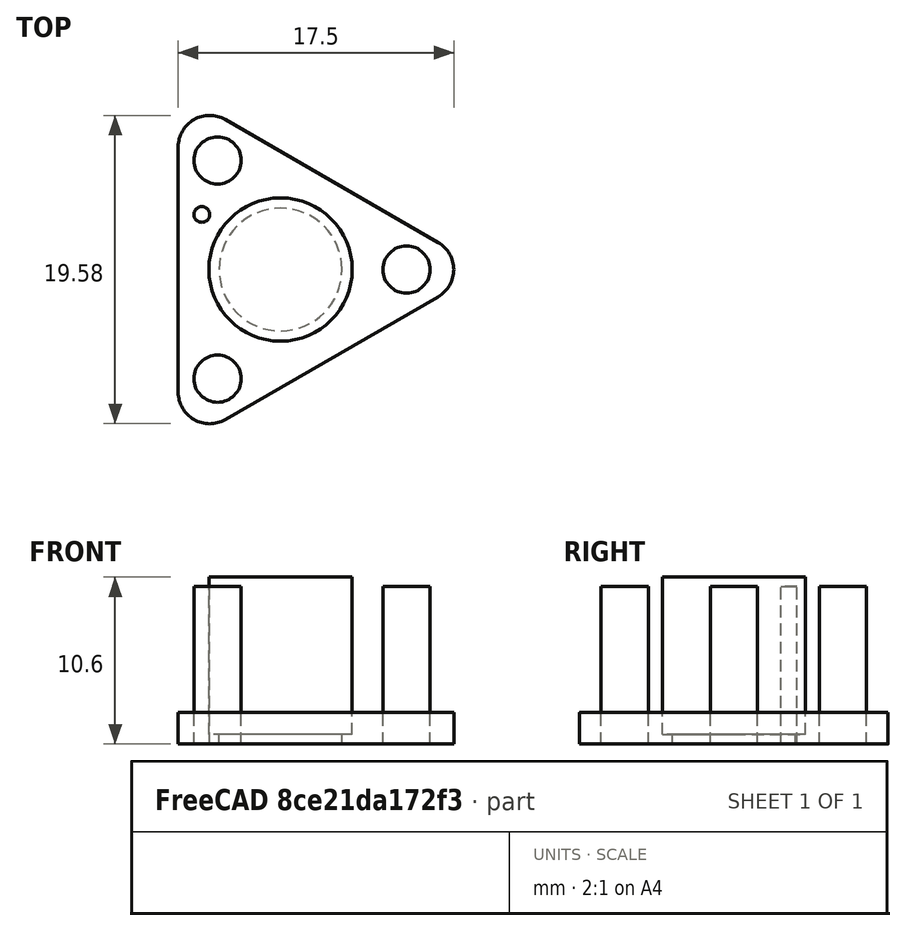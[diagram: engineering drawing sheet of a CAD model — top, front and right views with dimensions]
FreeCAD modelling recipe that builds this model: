
FCSTD DOCUMENT  (FreeCAD 0.18R16033 (Git))
Label: insulator_2
License: All rights reserved
LicenseURL: http://en.wikipedia.org/wiki/All_rights_reserved
objects: Part::Cylinder×4, Part::FeaturePython×2, Part::MultiFuse×2, PartDesign::AdditivePrism×1, Part::Fillet×1
note: 11 computed .brp shape members not serialized (recipe doc carries the construction recipe); baked Part::Feature solids carry a one-line shape summary decoded from their .brp

FEATURE [PartDesign::AdditivePrism] Prism
  AttacherType = Attacher::AttachEngine3D
  Circumradius = 13
  Height = 2
  Polygon = 3
FEATURE [Part::Cylinder] Cylinder055  label="WireWrap"
  Angle = 360
  AttacherType = Attacher::AttachEngine3D
  Height = 10
  Placement = pos=(-5,3.5,0) rot=(0,0,1;0rad)
  Radius = 0.5
  expr: Radius = 0.5
FEATURE [Part::FeaturePython] Array012  # Draft array (typed FeaturePython)
  Angle = 360
  ArrayType = 1
  Axis = (0,0,1)
  Base = -> Cylinder055
  Center = (0,0,0)
  Fuse = false
  IntervalAxis = (0,0,0)
  IntervalX = (1,0,0)
  IntervalY = (0,1,0)
  IntervalZ = (0,0,1)
  NumberPolar = 1
  NumberX = 2
  NumberY = 2
  NumberZ = 1
FEATURE [Part::Fillet] Fillet
  Base = -> Prism
  Edges = 3 edges r=2: [Edge1,Edge2,Edge5]
FEATURE [Part::Cylinder] Cylinder024  label="Cylinder016"
  Angle = 360
  AttacherType = Attacher::AttachEngine3D
  Height = 10
  Placement = pos=(8,0,0) rot=(0,0,1;0rad)
  Radius = 1.5
FEATURE [Part::FeaturePython] Array  # Draft array (typed FeaturePython)
  Angle = 360
  ArrayType = 1
  Axis = (0,0,1)
  Base = -> Cylinder024
  Center = (0,0,0)
  Fuse = false
  IntervalAxis = (0,0,0)
  IntervalX = (1,0,0)
  IntervalY = (0,1,0)
  IntervalZ = (0,0,1)
  NumberPolar = 3
  NumberX = 2
  NumberY = 2
  NumberZ = 1
FEATURE [Part::Cylinder] Cylinder026  label="MountPlateInnerHole"
  Angle = 360
  AttacherType = Attacher::AttachEngine3D
  Height = 10
  Radius = 3.9
FEATURE [Part::Cylinder] Cylinder027  label="MountPlateLip"
  Angle = 360
  AttacherType = Attacher::AttachEngine3D
  Height = 10
  Placement = pos=(0,0,0.6) rot=(0,0,1;0rad)
  Radius = 4.55
FEATURE [Part::MultiFuse] Fusion012
  Shapes = -> [Array,Cylinder027,Cylinder026]
FEATURE [Part::MultiFuse] Fusion014
  Shapes = -> [Fusion012,Array012]
